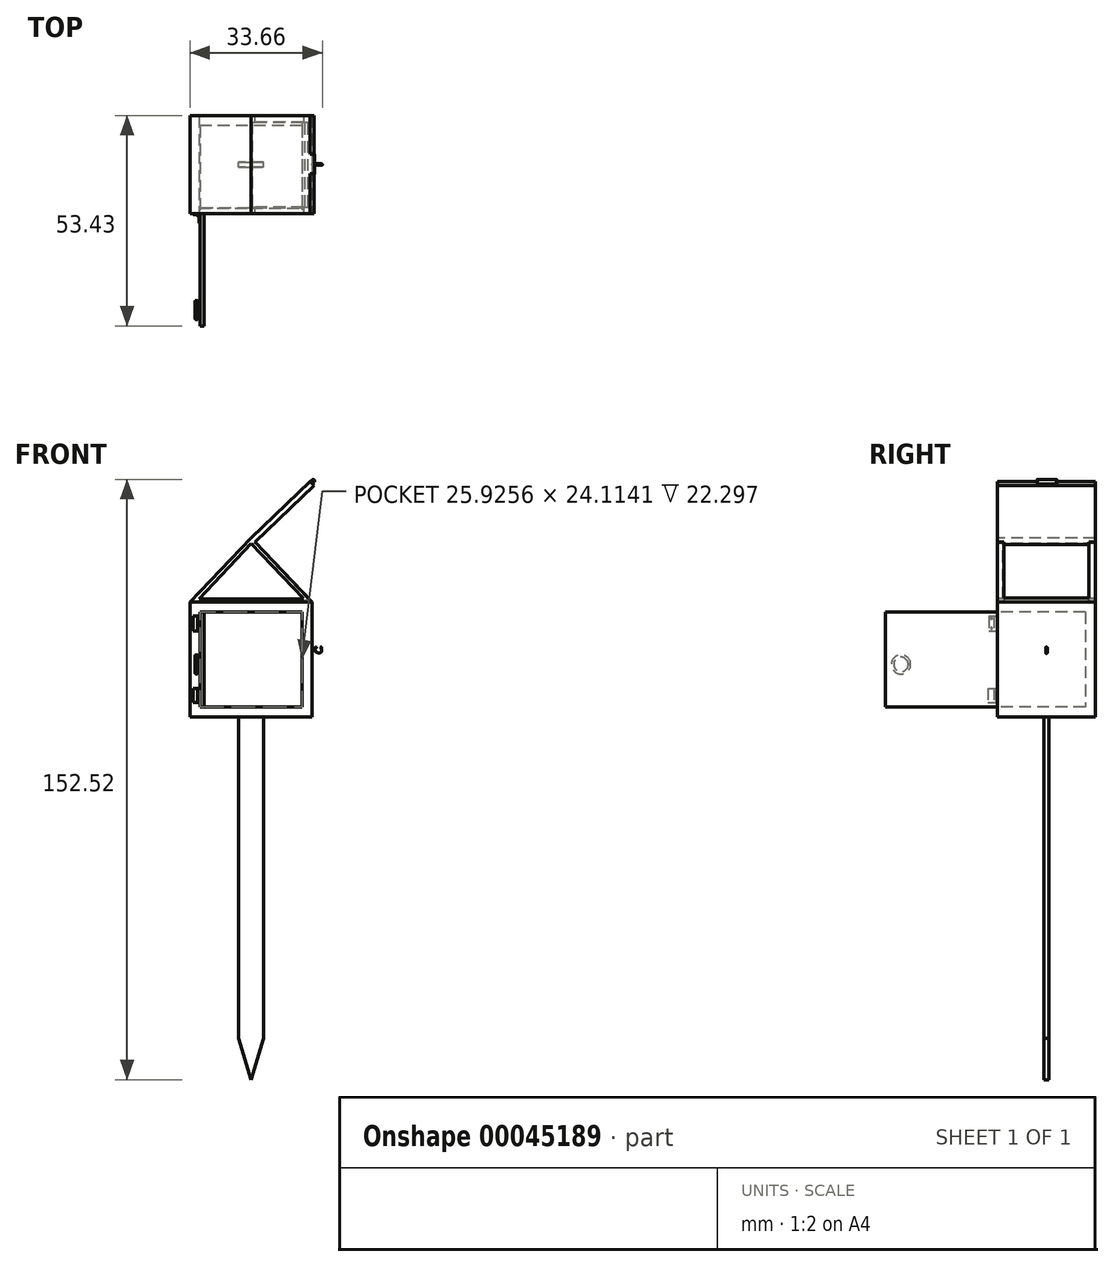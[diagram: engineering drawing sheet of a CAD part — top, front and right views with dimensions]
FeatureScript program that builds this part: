
annotation { "Feature Type Name" : "Feature", "Feature Type Description" : "" }
export const myFeature = defineFeature(function(context is Context, id is Id, definition is map)
    precondition{}
    {
        {
            var Q0;
            Q0=qCreatedBy(makeId("Front.planeOp"),FACE);
            var sketch = newSketch(context, id + "F0", { "sketchPlane" : qUnion([Q0])});
            skLineSegment(sketch, "E0.rect.top", {"start": v(3.2, 40.8) * mm, "end": v(-3.2, 40.8) * mm});
            skLineSegment(sketch, "E0.rect.left", {"start": v(3.2, -40.8) * mm, "end": v(3.2, 40.8) * mm});
            skLineSegment(sketch, "E0.rect.right", {"start": v(-3.2, -40.8) * mm, "end": v(-3.2, 40.8) * mm});
            skPoint(sketch, "E0.rect.middle", {"position": v(0, 0) * mm});
            skLineSegment(sketch, "E1", {"start": v(-3.2, -40.8) * mm, "end": v(0, -51.36) * mm});
            skLineSegment(sketch, "E2", {"start": v(0, -51.36) * mm, "end": v(3.2, -40.8) * mm});
            skSolve(sketch);
        }
        {
            var Q0;
            Q0 = qSketchRegion(id + "F0", true);
            extrude(context, id + "F1", {"entities" : qUnion([Q0]), "endBound" : BoundingType.SYMMETRIC, "depth" : 1.27 * mm});
        }
        {
            var Q0;
            Q0=makeQuery(id+"F1.opExtrude","SWEPT_FACE",FACE,{"disambiguationData":[OSD([sQuery(id+"F0.wireOp",EDGE,"E0.rect.top")])]});
            var sketch = newSketch(context, id + "F2", { "sketchPlane" : qUnion([Q0])});
            skLineSegment(sketch, "E3.rect.bottom", {"start": v(15.5, 12.42) * mm, "end": v(-15.5, 12.42) * mm});
            skLineSegment(sketch, "E3.rect.top", {"start": v(15.5, -12.42) * mm, "end": v(-15.5, -12.42) * mm});
            skLineSegment(sketch, "E3.rect.left", {"start": v(15.5, 12.42) * mm, "end": v(15.5, -12.42) * mm});
            skLineSegment(sketch, "E3.rect.right", {"start": v(-15.5, 12.42) * mm, "end": v(-15.5, -12.42) * mm});
            skPoint(sketch, "E3.rect.middle", {"position": v(0, 0) * mm});
            skSolve(sketch);
        }
        {
            var Q0;
            Q0 = qSketchRegion(id + "F2", true);
            extrude(context, id + "F3", {"entities" : qUnion([Q0]), "operationType" : NewBodyOperationType.ADD, "depth" : 29.2 * mm});
        }
        {
            var Q0;
            Q0=makeQuery(id+"F3.opExtrude","SWEPT_FACE",FACE,{"disambiguationData":[OSD([sQuery(id+"F2.wireOp",EDGE,"E3.rect.top")])]});
            var sketch = newSketch(context, id + "F4", { "sketchPlane" : qUnion([Q0])});
            skLineSegment(sketch, "E4", {"start": v(-15.5, 70) * mm, "end": v(0, 86.23) * mm});
            skLineSegment(sketch, "E5", {"start": v(0, 86.23) * mm, "end": v(15.5, 70) * mm});
            skSolve(sketch);
        }
        {
            var Q0;
            Q0 = qSketchRegion(id + "F4", true);
            var Q1;
            Q1=makeQuery(id+"F4.imprint","IMPRINT",FACE,{"disambiguationData":[TD([[makeQuery(id+"F4.imprint","IMPRINT",EDGE,{"derivedFrom":sQuery(id+"F4.wireOp",EDGE,"E4")}),-1.0]])]});
            extrude(context, id + "F5", {"entities" : qUnion([Q0, Q1]), "oppositeDirection" : true, "depth" : 24.87 * mm});
        }
        {
            var Q0;
            Q0=qCreatedBy(makeId("Front.planeOp"),FACE);
            var sketch = newSketch(context, id + "F6", { "sketchPlane" : qUnion([Q0])});
            skFitSpline(sketch, "E6", {"points": [v(15.43, 58.5) * mm, v(16.58, 58.49) * mm, v(16.65, 57.64) * mm, v(17.58, 57.35) * mm, v(17.72, 58) * mm, v(17.79, 58.63) * mm, v(18.07, 58.13) * mm, v(18, 57.07) * mm, v(16.72, 56.93) * mm, v(16.08, 57.42) * mm, v(16.01, 57.92) * mm, v(15.45, 57.7) * mm], "startDerivative": vector(14.13, 2.86) * mm, "endDerivative": vector(-9.24, -5.42) * mm});
            skLineSegment(sketch, "E7", {"start": v(15.43, 58.5) * mm, "end": v(15.45, 57.7) * mm});
            skSolve(sketch);
        }
        {
            var Q0;
            Q0 = qSketchRegion(id + "F6", true);
            extrude(context, id + "F7", {"entities" : qUnion([Q0]), "operationType" : NewBodyOperationType.ADD, "endBound" : BoundingType.SYMMETRIC, "depth" : 0.38 * mm});
        }
        {
            var Q0;
            Q0=makeQuery(id+"F7.opExtrude","CAP_EDGE",EDGE,{"disambiguationData":[OSD([sQuery(id+"F6.wireOp",EDGE,"E6")])],"isStart":false});
            var Q1;
            Q1=makeQuery(id+"F7.opExtrude","CAP_EDGE",EDGE,{"disambiguationData":[OSD([sQuery(id+"F6.wireOp",EDGE,"E6")])],"isStart":true});
            fillet(context, id + "F8", {"entities" : qUnion([Q0, Q1]), "radius" : 0.25 * mm, "tangentPropagation" : true, "allowEdgeOverflow" : false});
        }
        {
            var Q0;
            Q0=makeQuery(id+"F3.opExtrude","SWEPT_FACE",FACE,{"disambiguationData":[OSD([sQuery(id+"F2.wireOp",EDGE,"E3.rect.top")])]});
            shell(context, id + "F9", {"entities" : qUnion([Q0]), "thickness" : 2.54 * mm});
        }
        {
            var Q0;
            Q0=makeQuery(id+"F3.opExtrude","SWEPT_FACE",FACE,{"disambiguationData":[OSD([sQuery(id+"F2.wireOp",EDGE,"E3.rect.top")])]});
            var sketch = newSketch(context, id + "F10", { "sketchPlane" : qUnion([Q0])});
            skLineSegment(sketch, "E8.bottom", {"start": v(-12.96, 67.46) * mm, "end": v(-11.96, 67.46) * mm});
            skLineSegment(sketch, "E8.top", {"start": v(-12.96, 43.35) * mm, "end": v(-11.96, 43.35) * mm});
            skLineSegment(sketch, "E8.left", {"start": v(-12.96, 67.46) * mm, "end": v(-12.96, 43.35) * mm});
            skLineSegment(sketch, "E8.right", {"start": v(-11.96, 67.46) * mm, "end": v(-11.96, 43.35) * mm});
            skSolve(sketch);
        }
        {
            var Q0;
            Q0=makeQuery(id+"F10.imprint","IMPRINT",FACE,{"disambiguationData":[TD([[makeQuery(id+"F10.imprint","IMPRINT",EDGE,{"derivedFrom":sQuery(id+"F10.wireOp",EDGE,"E8.bottom")}),1.0]])]});
            extrude(context, id + "F11", {"entities" : qUnion([Q0]), "depth" : 28.56 * mm});
        }
        {
            var Q0;
            Q0=makeQuery(id+"F11.opExtrude","SWEPT_FACE",FACE,{"disambiguationData":[OSD([sQuery(id+"F10.wireOp",EDGE,"E8.left")])]});
            var sketch = newSketch(context, id + "F12", { "sketchPlane" : qUnion([Q0])});
            skCircle(sketch, "E9", {"center": v(36.95, 54.15) * mm, "radius": 1.84 * mm});
            skSolve(sketch);
        }
        {
            var Q0;
            Q0 = qSketchRegion(id + "F12", true);
            var Q1;
            Q1=makeQuery(id+"F12.imprint","IMPRINT",FACE,{"disambiguationData":[TD([[makeQuery(id+"F12.imprint","IMPRINT",EDGE,{"derivedFrom":sQuery(id+"F12.wireOp",EDGE,"E9")}),1.0]])]});
            extrude(context, id + "F13", {"entities" : qUnion([Q0, Q1]), "operationType" : NewBodyOperationType.ADD, "depth" : 0.52 * mm});
        }
        {
            var Q0;
            Q0=makeQuery(id+"F13.opExtrude","CAP_FACE",FACE,{"disambiguationData":[OSD([sQuery(id+"F12.wireOp",EDGE,"E9")])],"isStart":false});
            var sketch = newSketch(context, id + "F14", { "sketchPlane" : qUnion([Q0])});
            skCircle(sketch, "E10", {"center": v(36.95, 54.15) * mm, "radius": 2.45 * mm});
            skSolve(sketch);
        }
        {
            var Q0;
            Q0=makeQuery(id+"F14.imprint","IMPRINT",FACE,{"disambiguationData":[TD([[makeQuery(id+"F14.imprint","IMPRINT",EDGE,{"derivedFrom":sQuery(id+"F14.wireOp",EDGE,"E10")}),1.0]])]});
            var Q1;
            Q1=makeQuery(id+"F14.imprint","IMPRINT",FACE,{"disambiguationData":[TD([[makeQuery(id+"F14.imprint","IMPRINT",EDGE,{"derivedFrom":makeQuery(id+"F13.opExtrude","CAP_EDGE",EDGE,{"disambiguationData":[OSD([sQuery(id+"F12.wireOp",EDGE,"E9")])],"isStart":false})}),1.0]])]});
            extrude(context, id + "F15", {"entities" : qUnion([Q0, Q1]), "operationType" : NewBodyOperationType.ADD, "depth" : 0.73 * mm});
        }
        {
            var Q0;
            Q0=makeQuery(id+"F15.opExtrude","CAP_EDGE",EDGE,{"disambiguationData":[OSD([sQuery(id+"F14.wireOp",EDGE,"E10")])],"isStart":false});
            var Q1;
            Q1=makeQuery(id+"F15.opExtrude","CAP_EDGE",EDGE,{"disambiguationData":[OSD([sQuery(id+"F14.wireOp",EDGE,"E10")])],"isStart":true});
            fillet(context, id + "F16", {"entities" : qUnion([Q0, Q1]), "radius" : 0.3 * mm, "tangentPropagation" : true, "allowEdgeOverflow" : false});
        }
        {
            var Q0;
            Q0=makeQuery(id+"F3.opExtrude","SWEPT_FACE",FACE,{"disambiguationData":[OSD([sQuery(id+"F2.wireOp",EDGE,"E3.rect.top")])]});
            var sketch = newSketch(context, id + "F17", { "sketchPlane" : qUnion([Q0])});
            skLineSegment(sketch, "E11.bottom", {"start": v(-12.96, 66.39) * mm, "end": v(-13.62, 66.39) * mm});
            skLineSegment(sketch, "E11.top", {"start": v(-12.96, 62.7) * mm, "end": v(-13.62, 62.7) * mm});
            skLineSegment(sketch, "E11.left", {"start": v(-12.96, 66.39) * mm, "end": v(-12.96, 62.7) * mm});
            skLineSegment(sketch, "E11.right", {"start": v(-13.62, 66.39) * mm, "end": v(-13.62, 62.7) * mm});
            skLineSegment(sketch, "E12.bottom", {"start": v(-12.96, 44.53) * mm, "end": v(-13.62, 44.53) * mm});
            skLineSegment(sketch, "E12.top", {"start": v(-12.96, 48.1) * mm, "end": v(-13.62, 48.1) * mm});
            skLineSegment(sketch, "E12.left", {"start": v(-12.96, 44.53) * mm, "end": v(-12.96, 48.1) * mm});
            skLineSegment(sketch, "E12.right", {"start": v(-13.62, 44.53) * mm, "end": v(-13.62, 48.1) * mm});
            skSolve(sketch);
        }
        {
            var Q0;
            Q0 = qSketchRegion(id + "F17", true);
            extrude(context, id + "F18", {"entities" : qUnion([Q0]), "depth" : 1 * mm});
        }
        {
            var Q0;
            Q0=makeQuery(id+"F18.opExtrude","CAP_FACE",FACE,{"disambiguationData":[OSD([sQuery(id+"F17.wireOp",EDGE,"E11.bottom"),sQuery(id+"F17.wireOp",EDGE,"E11.top"),sQuery(id+"F17.wireOp",EDGE,"E11.left"),sQuery(id+"F17.wireOp",EDGE,"E11.right")])],"isStart":false});
            var sketch = newSketch(context, id + "F19", { "sketchPlane" : qUnion([Q0])});
            skLineSegment(sketch, "E13.bottom", {"start": v(-12.96, 66.39) * mm, "end": v(-13.12, 66.39) * mm});
            skLineSegment(sketch, "E13.top", {"start": v(-12.96, 62.7) * mm, "end": v(-13.12, 62.7) * mm});
            skLineSegment(sketch, "E13.left", {"start": v(-12.96, 66.39) * mm, "end": v(-12.96, 62.7) * mm});
            skLineSegment(sketch, "E13.right", {"start": v(-13.12, 66.39) * mm, "end": v(-13.12, 62.7) * mm});
            skSolve(sketch);
        }
        {
            var Q0;
            Q0 = qSketchRegion(id + "F19", true);
            extrude(context, id + "F20", {"entities" : qUnion([Q0]), "depth" : 1.24 * mm});
        }
        {
            var Q0;
            Q0=makeQuery(id+"F18.opExtrude","SWEPT_FACE",FACE,{"disambiguationData":[OSD([sQuery(id+"F17.wireOp",EDGE,"E11.right")])]});
            var sketch = newSketch(context, id + "F21", { "sketchPlane" : qUnion([Q0])});
            skLineSegment(sketch, "E14.bottom", {"start": v(12.42, 66.39) * mm, "end": v(12.64, 66.39) * mm});
            skLineSegment(sketch, "E14.top", {"start": v(12.42, 62.7) * mm, "end": v(12.64, 62.7) * mm});
            skLineSegment(sketch, "E14.left", {"start": v(12.42, 66.39) * mm, "end": v(12.42, 62.7) * mm});
            skLineSegment(sketch, "E14.right", {"start": v(12.64, 66.39) * mm, "end": v(12.64, 62.7) * mm});
            skSolve(sketch);
        }
        {
            var Q0;
            Q0 = qSketchRegion(id + "F21", true);
            extrude(context, id + "F22", {"entities" : qUnion([Q0]), "depth" : 1.04 * mm});
        }
        {
            var Q0;
            Q0=makeQuery(id+"F18.opExtrude","CAP_FACE",FACE,{"disambiguationData":[OSD([sQuery(id+"F17.wireOp",EDGE,"E12.bottom"),sQuery(id+"F17.wireOp",EDGE,"E12.top"),sQuery(id+"F17.wireOp",EDGE,"E12.left"),sQuery(id+"F17.wireOp",EDGE,"E12.right")])],"isStart":false});
            var sketch = newSketch(context, id + "F23", { "sketchPlane" : qUnion([Q0])});
            skLineSegment(sketch, "E15.bottom", {"start": v(-12.96, 48.1) * mm, "end": v(-13.13, 48.1) * mm});
            skLineSegment(sketch, "E15.top", {"start": v(-12.96, 44.53) * mm, "end": v(-13.13, 44.53) * mm});
            skLineSegment(sketch, "E15.left", {"start": v(-12.96, 48.1) * mm, "end": v(-12.96, 44.53) * mm});
            skLineSegment(sketch, "E16", {"start": v(-13.13, 48.1) * mm, "end": v(-13.13, 44.53) * mm});
            skPoint(sketch, "E17.orphan", {"position": v(-13.3, 48.1) * mm});
            skPoint(sketch, "E18.orphan", {"position": v(-13.3, 44.53) * mm});
            skSolve(sketch);
        }
        {
            var Q0;
            Q0 = qSketchRegion(id + "F23", true);
            extrude(context, id + "F24", {"entities" : qUnion([Q0]), "depth" : 1.42 * mm});
        }
        {
            var Q0;
            Q0=makeQuery(id+"F18.opExtrude","SWEPT_FACE",FACE,{"disambiguationData":[OSD([sQuery(id+"F17.wireOp",EDGE,"E12.right")])]});
            var sketch = newSketch(context, id + "F25", { "sketchPlane" : qUnion([Q0])});
            skLineSegment(sketch, "E19.bottom", {"start": v(12.42, 48.1) * mm, "end": v(12.67, 48.1) * mm});
            skLineSegment(sketch, "E19.top", {"start": v(12.42, 44.53) * mm, "end": v(12.67, 44.53) * mm});
            skLineSegment(sketch, "E19.left", {"start": v(12.42, 48.1) * mm, "end": v(12.42, 44.53) * mm});
            skLineSegment(sketch, "E20", {"start": v(12.67, 44.53) * mm, "end": v(12.67, 48.1) * mm});
            skPoint(sketch, "E19.right.start.orphan", {"position": v(12.91, 48.1) * mm});
            skPoint(sketch, "E21.orphan", {"position": v(12.91, 44.53) * mm});
            skSolve(sketch);
        }
        {
            var Q0;
            Q0 = qSketchRegion(id + "F25", true);
            extrude(context, id + "F26", {"entities" : qUnion([Q0]), "depth" : 1.06 * mm});
        }
        {
            var Q0;
            Q0=makeQuery(id+"F18.opExtrude","CAP_EDGE",EDGE,{"disambiguationData":[OSD([sQuery(id+"F17.wireOp",EDGE,"E11.right")])],"isStart":false});
            var Q1;
            Q1=makeQuery(id+"F18.opExtrude","CAP_EDGE",EDGE,{"disambiguationData":[OSD([sQuery(id+"F17.wireOp",EDGE,"E12.right")])],"isStart":false});
            fillet(context, id + "F27", {"entities" : qUnion([Q0, Q1]), "radius" : 0.76 * mm, "tangentPropagation" : true, "allowEdgeOverflow" : false});
        }
        {
            var Q0;
            Q0=makeQuery(id+"F20.opExtrude","SWEPT_FACE",FACE,{"disambiguationData":[OSD([sQuery(id+"F19.wireOp",EDGE,"E13.right")])]});
            var sketch = newSketch(context, id + "F28", { "sketchPlane" : qUnion([Q0])});
            skCircle(sketch, "E22", {"center": v(13.97, 65.83) * mm, "radius": 0.2 * mm});
            skCircle(sketch, "E23", {"center": v(13.97, 63.33) * mm, "radius": 0.19 * mm});
            skSolve(sketch);
        }
        {
            var Q0;
            Q0 = qSketchRegion(id + "F28", true);
            extrude(context, id + "F29", {"entities" : qUnion([Q0]), "operationType" : NewBodyOperationType.ADD, "depth" : 0.04 * mm});
        }
        {
            var Q0;
            Q0=makeQuery(id+"F29.opExtrude","CAP_EDGE",EDGE,{"disambiguationData":[OSD([sQuery(id+"F28.wireOp",EDGE,"E23")])],"isStart":false});
            var Q1;
            Q1=makeQuery(id+"F29.opExtrude","CAP_EDGE",EDGE,{"disambiguationData":[OSD([sQuery(id+"F28.wireOp",EDGE,"E22")])],"isStart":false});
            var Q2;
            Q2=makeQuery(id+"FZxubR1NUOaGF2b_9.opExtrude","CAP_EDGE",EDGE,{"disambiguationData":[OSD([sQuery(id+"F324GHYX8C8gesv_9.wireOp",EDGE,"1a2da487-a73d-43d1-b490-06fb37f9b1f9")])],"isStart":false});
            var Q3;
            Q3=makeQuery(id+"FZxubR1NUOaGF2b_9.opExtrude","CAP_EDGE",EDGE,{"disambiguationData":[OSD([sQuery(id+"F324GHYX8C8gesv_9.wireOp",EDGE,"9afe2487-ca41-400e-9fc8-1148ac821239")])],"isStart":false});
            fillet(context, id + "F30", {"entities" : qUnion([Q0, Q1, Q2, Q3]), "radius" : 0.25 * mm, "tangentPropagation" : true, "allowEdgeOverflow" : false});
        }
        {
            var Q0;
            Q0=makeQuery(id+"F5.opExtrude","CAP_FACE",FACE,{"disambiguationData":[OSD([sQuery(id+"F2.wireOp",EDGE,"E3.rect.top"),sQuery(id+"F4.wireOp",EDGE,"E4"),sQuery(id+"F4.wireOp",EDGE,"E5")])],"isStart":true});
            var sketch = newSketch(context, id + "F31", { "sketchPlane" : qUnion([Q0])});
            skLineSegment(sketch, "E24", {"start": v(-13.18, 70.82) * mm, "end": v(0, 84.92) * mm});
            skLineSegment(sketch, "E25", {"start": v(0, 84.92) * mm, "end": v(13.34, 70.88) * mm});
            skLineSegment(sketch, "E26", {"start": v(13.34, 70.88) * mm, "end": v(-13.18, 70.82) * mm});
            skSolve(sketch);
        }
        {
            var Q0;
            Q0 = qSketchRegion(id + "F31", true);
            extrude(context, id + "F32", {"entities" : qUnion([Q0]), "operationType" : NewBodyOperationType.REMOVE, "oppositeDirection" : true, "depth" : 24.8 * mm});
        }
        {
            var Q0;
            Q0=makeQuery(id+"F5.opExtrude","SWEPT_FACE",FACE,{"disambiguationData":[OSD([sQuery(id+"F4.wireOp",EDGE,"E5")])]});
            var sketch = newSketch(context, id + "F33", { "sketchPlane" : qUnion([Q0])});
            skLineSegment(sketch, "E27.bottom", {"start": v(-10.8, 60.91) * mm, "end": v(10.74, 60.91) * mm});
            skLineSegment(sketch, "E27.top", {"start": v(-10.8, 41.3) * mm, "end": v(10.74, 41.3) * mm});
            skLineSegment(sketch, "E27.left", {"start": v(-10.8, 60.91) * mm, "end": v(-10.8, 41.3) * mm});
            skLineSegment(sketch, "E27.right", {"start": v(10.74, 60.91) * mm, "end": v(10.74, 41.3) * mm});
            skSolve(sketch);
        }
        {
            var Q0;
            Q0=makeQuery(id+"F33.imprint","IMPRINT",FACE,{"disambiguationData":[TD([[makeQuery(id+"F33.imprint","IMPRINT",EDGE,{"derivedFrom":sQuery(id+"F33.wireOp",EDGE,"E27.bottom")}),-1.0]])]});
            extrude(context, id + "F34", {"entities" : qUnion([Q0]), "operationType" : NewBodyOperationType.REMOVE, "oppositeDirection" : true, "depth" : 1.14 * mm});
        }
        {
            var Q0;
            Q0=makeQuery(id+"F5.opExtrude","CAP_FACE",FACE,{"disambiguationData":[OSD([sQuery(id+"F2.wireOp",EDGE,"E3.rect.top"),sQuery(id+"F4.wireOp",EDGE,"E4"),sQuery(id+"F4.wireOp",EDGE,"E5")])],"isStart":true});
            var sketch = newSketch(context, id + "F35", { "sketchPlane" : qUnion([Q0])});
            skLineSegment(sketch, "E28", {"start": v(-13.18, 70.82) * mm, "end": v(0, 84.92) * mm});
            skLineSegment(sketch, "E29", {"start": v(0, 84.92) * mm, "end": v(13.34, 70.88) * mm});
            skLineSegment(sketch, "E30", {"start": v(13.34, 70.88) * mm, "end": v(-13.18, 70.82) * mm});
            skSolve(sketch);
        }
        {
            var Q0;
            Q0=makeQuery(id+"F35.imprint","IMPRINT",FACE,{"disambiguationData":[TD([[makeQuery(id+"F35.imprint","IMPRINT",EDGE,{"derivedFrom":sQuery(id+"F35.wireOp",EDGE,"E28")}),-1.0]])]});
            extrude(context, id + "F36", {"entities" : qUnion([Q0]), "oppositeDirection" : true, "depth" : 1.4 * mm});
        }
        {
            var Q0;
            Q0=makeQuery(id+"F5.opExtrude","SWEPT_FACE",FACE,{"disambiguationData":[OSD([sQuery(id+"F4.wireOp",EDGE,"E5")])]});
            var sketch = newSketch(context, id + "F37", { "sketchPlane" : qUnion([Q0])});
            skLineSegment(sketch, "E31.bottom", {"start": v(-12.42, 62.35) * mm, "end": v(12.45, 62.35) * mm});
            skLineSegment(sketch, "E31.top", {"start": v(-12.42, 60.91) * mm, "end": v(12.45, 60.91) * mm});
            skLineSegment(sketch, "E31.left", {"start": v(-12.42, 62.35) * mm, "end": v(-12.42, 60.91) * mm});
            skLineSegment(sketch, "E31.right", {"start": v(12.45, 62.35) * mm, "end": v(12.45, 60.91) * mm});
            skSolve(sketch);
        }
        {
            var Q0;
            Q0 = qSketchRegion(id + "F37", true);
            extrude(context, id + "F38", {"entities" : qUnion([Q0]), "operationType" : NewBodyOperationType.ADD, "depth" : 20.78 * mm});
        }
        {
            var Q0;
            Q0=makeQuery(id+"F38.opExtrude","CAP_FACE",FACE,{"disambiguationData":[OSD([sQuery(id+"F37.wireOp",EDGE,"E31.bottom"),sQuery(id+"F37.wireOp",EDGE,"E31.top"),sQuery(id+"F37.wireOp",EDGE,"E31.left"),sQuery(id+"F37.wireOp",EDGE,"E31.right")])],"isStart":false});
            var sketch = newSketch(context, id + "F39", { "sketchPlane" : qUnion([Q0])});
            skLineSegment(sketch, "E32.bottom", {"start": v(-2.34, 62.35) * mm, "end": v(2.6, 62.35) * mm});
            skLineSegment(sketch, "E32.top", {"start": v(-2.34, 61.53) * mm, "end": v(2.6, 61.53) * mm});
            skLineSegment(sketch, "E32.left", {"start": v(-2.34, 62.35) * mm, "end": v(-2.34, 61.53) * mm});
            skLineSegment(sketch, "E32.right", {"start": v(2.6, 62.35) * mm, "end": v(2.6, 61.53) * mm});
            skSolve(sketch);
        }
        {
            var Q0;
            Q0 = qSketchRegion(id + "F39", true);
            extrude(context, id + "F40", {"entities" : qUnion([Q0]), "operationType" : NewBodyOperationType.ADD, "depth" : 1.06 * mm});
        }
        {
            var Q0;
            Q0=makeQuery(id+"F40.opExtrude","CAP_EDGE",EDGE,{"disambiguationData":[OSD([sQuery(id+"F39.wireOp",EDGE,"E32.top")])],"isStart":false});
            var Q1;
            Q1=makeQuery(id+"F40.opExtrude","CAP_EDGE",EDGE,{"disambiguationData":[OSD([sQuery(id+"F39.wireOp",EDGE,"E32.bottom")])],"isStart":false});
            var Q2;
            Q2=makeQuery(id+"F40.opExtrude","CAP_EDGE",EDGE,{"disambiguationData":[OSD([sQuery(id+"F39.wireOp",EDGE,"E32.left")])],"isStart":false});
            var Q3;
            Q3=makeQuery(id+"F40.opExtrude","CAP_EDGE",EDGE,{"disambiguationData":[OSD([sQuery(id+"F39.wireOp",EDGE,"E32.right")])],"isStart":false});
            fillet(context, id + "F41", {"entities" : qUnion([Q0, Q1, Q2, Q3]), "radius" : 0.38 * mm, "tangentPropagation" : true, "allowEdgeOverflow" : false});
        }
    });
